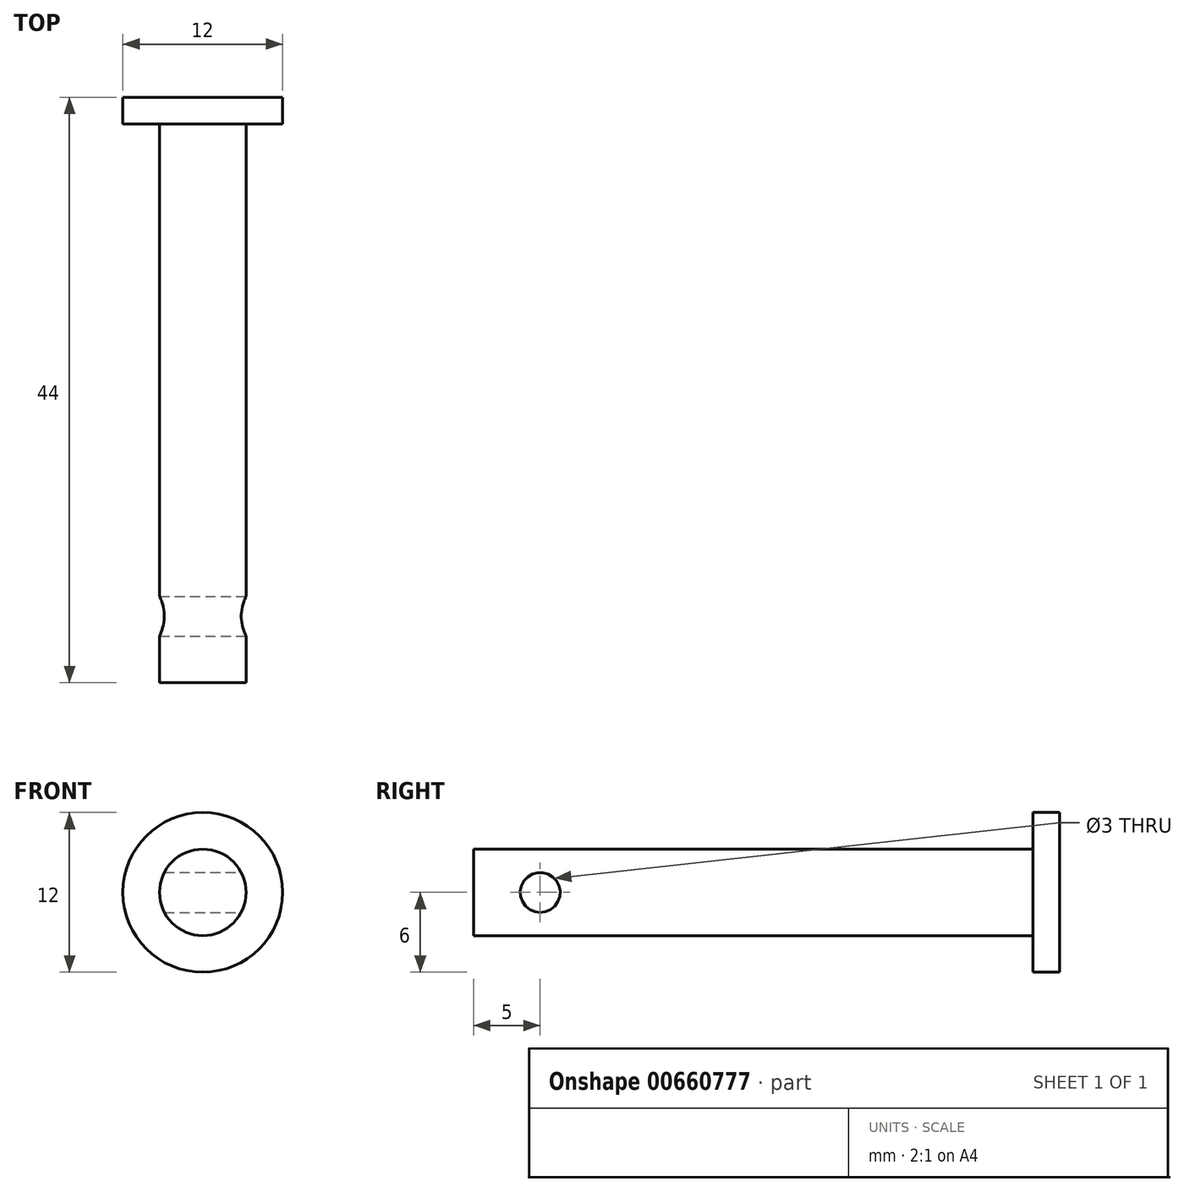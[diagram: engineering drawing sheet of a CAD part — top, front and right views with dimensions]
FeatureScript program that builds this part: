
annotation { "Feature Type Name" : "Feature", "Feature Type Description" : "" }
export const myFeature = defineFeature(function(context is Context, id is Id, definition is map)
    precondition{}
    {
        {
            var Q0;
            Q0=qCreatedBy(makeId("Front.planeOp"),FACE);
            var sketch = newSketch(context, id + "F0", { "sketchPlane" : qUnion([Q0])});
            skCircle(sketch, "E0", {"center": v(0, 0) * mm, "radius": 6 * mm});
            skCircle(sketch, "E1", {"center": v(0, 0) * mm, "radius": 3.25 * mm});
            skSolve(sketch);
        }
        {
            var Q0;
            Q0=makeQuery(id+"F0.imprint","IMPRINT",FACE,{"disambiguationData":[TD([[makeQuery(id+"F0.imprint","IMPRINT",EDGE,{"derivedFrom":sQuery(id+"F0.wireOp",EDGE,"E1")}),1.0]])]});
            extrude(context, id + "F1", {"entities" : qUnion([Q0]), "depth" : 44 * mm, "offsetDistance" : 25 * mm});
        }
        {
            var Q0;
            Q0 = qSketchRegion(id + "F0", true);
            extrude(context, id + "F2", {"entities" : qUnion([Q0]), "operationType" : NewBodyOperationType.ADD, "depth" : 2 * mm, "offsetDistance" : 25 * mm});
        }
        {
            var Q0;
            Q0=qCreatedBy(makeId("Right.planeOp"),FACE);
            var sketch = newSketch(context, id + "F3", { "sketchPlane" : qUnion([Q0])});
            skCircle(sketch, "E2", {"center": v(-39, 0) * mm, "radius": 1.5 * mm});
            skSolve(sketch);
        }
        {
            var Q0;
            Q0 = qSketchRegion(id + "F3", true);
            extrude(context, id + "F4", {"entities" : qUnion([Q0]), "operationType" : NewBodyOperationType.REMOVE, "endBound" : BoundingType.SYMMETRIC, "oppositeDirection" : true, "depth" : 10 * mm, "offsetDistance" : 25 * mm});
        }
    });
